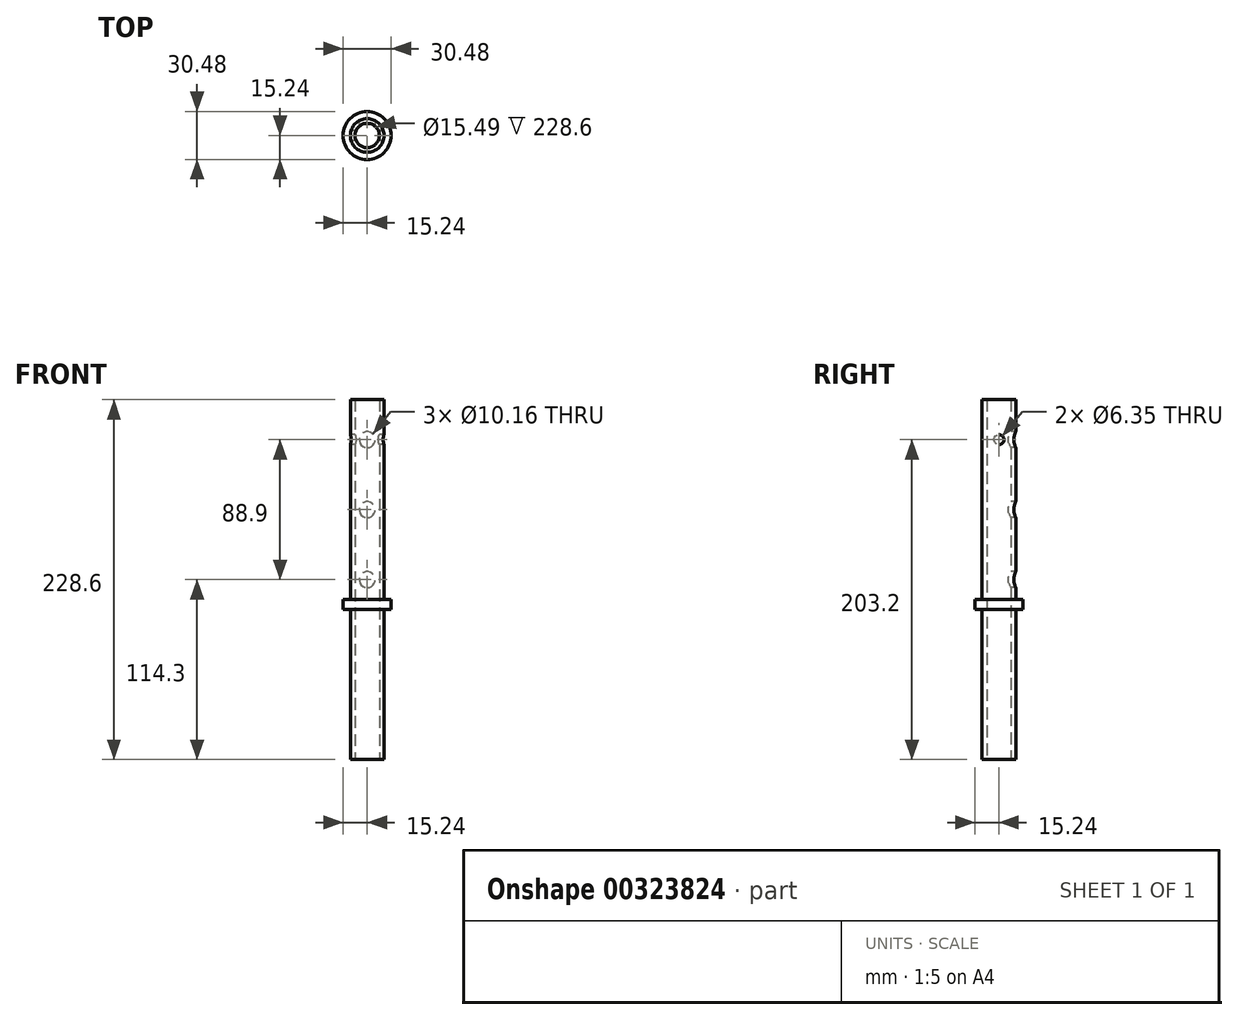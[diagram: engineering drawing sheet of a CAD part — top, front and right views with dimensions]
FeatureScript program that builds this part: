
annotation { "Feature Type Name" : "Feature", "Feature Type Description" : "" }
export const myFeature = defineFeature(function(context is Context, id is Id, definition is map)
    precondition{}
    {
        {
            var Q0;
            Q0=qCreatedBy(makeId("Top.planeOp"),FACE);
            var sketch = newSketch(context, id + "F0", { "sketchPlane" : qUnion([Q0])});
            skCircle(sketch, "E0", {"center": v(0, 0) * mm, "radius": 10.67 * mm});
            skCircle(sketch, "E1", {"center": v(0, 0) * mm, "radius": 7.75 * mm});
            skSolve(sketch);
        }
        {
            var Q0;
            Q0=makeQuery(id+"F0.imprint","IMPRINT",FACE,{"disambiguationData":[TD([[makeQuery(id+"F0.imprint","IMPRINT",EDGE,{"derivedFrom":sQuery(id+"F0.wireOp",EDGE,"E0")}),1.0]])]});
            extrude(context, id + "F1", {"entities" : qUnion([Q0]), "depth" : 95.25 * mm});
        }
        {
            var Q0;
            Q0=makeQuery(id+"F1.opExtrude","CAP_FACE",FACE,{"disambiguationData":[OSD([sQuery(id+"F0.wireOp",EDGE,"E0"),sQuery(id+"F0.wireOp",EDGE,"E1")])],"isStart":false});
            var sketch = newSketch(context, id + "F2", { "sketchPlane" : qUnion([Q0])});
            skCircle(sketch, "E2", {"center": v(0, 0) * mm, "radius": 15.24 * mm});
            skSolve(sketch);
        }
        {
            var Q0;
            Q0=makeQuery(id+"F2.imprint","IMPRINT",FACE,{"disambiguationData":[TD([[makeQuery(id+"F2.imprint","IMPRINT",EDGE,{"derivedFrom":sQuery(id+"F2.wireOp",EDGE,"E2")}),1.0]])]});
            var Q1;
            Q1=makeQuery(id+"F2.imprint","IMPRINT",FACE,{"disambiguationData":[TD([[makeQuery(id+"F2.imprint","IMPRINT",EDGE,{"derivedFrom":makeQuery(id+"F1.opExtrude","CAP_EDGE",EDGE,{"disambiguationData":[OSD([sQuery(id+"F0.wireOp",EDGE,"E0")])],"isStart":false})}),1.0]])]});
            extrude(context, id + "F3", {"entities" : qUnion([Q0, Q1]), "operationType" : NewBodyOperationType.ADD, "depth" : 6.35 * mm});
        }
        {
            var Q0;
            Q0=makeQuery(id+"F3.opExtrude","CAP_FACE",FACE,{"disambiguationData":[OSD([sQuery(id+"F0.wireOp",EDGE,"E1"),sQuery(id+"F2.wireOp",EDGE,"E2")])],"isStart":false});
            var sketch = newSketch(context, id + "F4", { "sketchPlane" : qUnion([Q0])});
            skCircle(sketch, "E3", {"center": v(0, 0) * mm, "radius": 10.67 * mm});
            skSolve(sketch);
        }
        {
            var Q0;
            Q0=makeQuery(id+"F4.imprint","IMPRINT",FACE,{"disambiguationData":[TD([[makeQuery(id+"F4.imprint","IMPRINT",EDGE,{"derivedFrom":sQuery(id+"F4.wireOp",EDGE,"E3")}),1.0]])]});
            extrude(context, id + "F5", {"entities" : qUnion([Q0]), "operationType" : NewBodyOperationType.ADD, "depth" : 127 * mm});
        }
        {
            var Q0;
            Q0=qCreatedBy(makeId("Right.planeOp"),FACE);
            var sketch = newSketch(context, id + "F6", { "sketchPlane" : qUnion([Q0])});
            skCircle(sketch, "E4", {"center": v(0, 203.2) * mm, "radius": 3.18 * mm});
            skSolve(sketch);
        }
        {
            var Q0;
            Q0=makeQuery(id+"F6.imprint","IMPRINT",FACE,{"disambiguationData":[TD([[makeQuery(id+"F6.imprint","IMPRINT",EDGE,{"derivedFrom":sQuery(id+"F6.wireOp",EDGE,"E4")}),1.0]])]});
            extrude(context, id + "F7", {"entities" : qUnion([Q0]), "operationType" : NewBodyOperationType.REMOVE, "endBound" : BoundingType.SYMMETRIC, "depth" : 25.4 * mm});
        }
        {
            var Q0;
            Q0=qCreatedBy(makeId("Front.planeOp"),FACE);
            var sketch = newSketch(context, id + "F8", { "sketchPlane" : qUnion([Q0])});
            skCircle(sketch, "E5", {"center": v(0, 203.2) * mm, "radius": 5.08 * mm});
            skCircle(sketch, "E6", {"center": v(0, 158.75) * mm, "radius": 5.08 * mm});
            skCircle(sketch, "E7", {"center": v(0, 114.3) * mm, "radius": 5.08 * mm});
            skSolve(sketch);
        }
        {
            var Q0;
            Q0=makeQuery(id+"F8.imprint","IMPRINT",FACE,{"disambiguationData":[TD([[makeQuery(id+"F8.imprint","IMPRINT",EDGE,{"derivedFrom":sQuery(id+"F8.wireOp",EDGE,"E7")}),1.0]])]});
            var Q1;
            Q1=makeQuery(id+"F8.imprint","IMPRINT",FACE,{"disambiguationData":[TD([[makeQuery(id+"F8.imprint","IMPRINT",EDGE,{"derivedFrom":sQuery(id+"F8.wireOp",EDGE,"E6")}),1.0]])]});
            var Q2;
            Q2=makeQuery(id+"F8.imprint","IMPRINT",FACE,{"disambiguationData":[TD([[makeQuery(id+"F8.imprint","IMPRINT",EDGE,{"derivedFrom":sQuery(id+"F8.wireOp",EDGE,"E5")}),1.0]])]});
            extrude(context, id + "F9", {"entities" : qUnion([Q0, Q1, Q2]), "operationType" : NewBodyOperationType.REMOVE, "oppositeDirection" : true, "depth" : 25.4 * mm});
        }
    });
